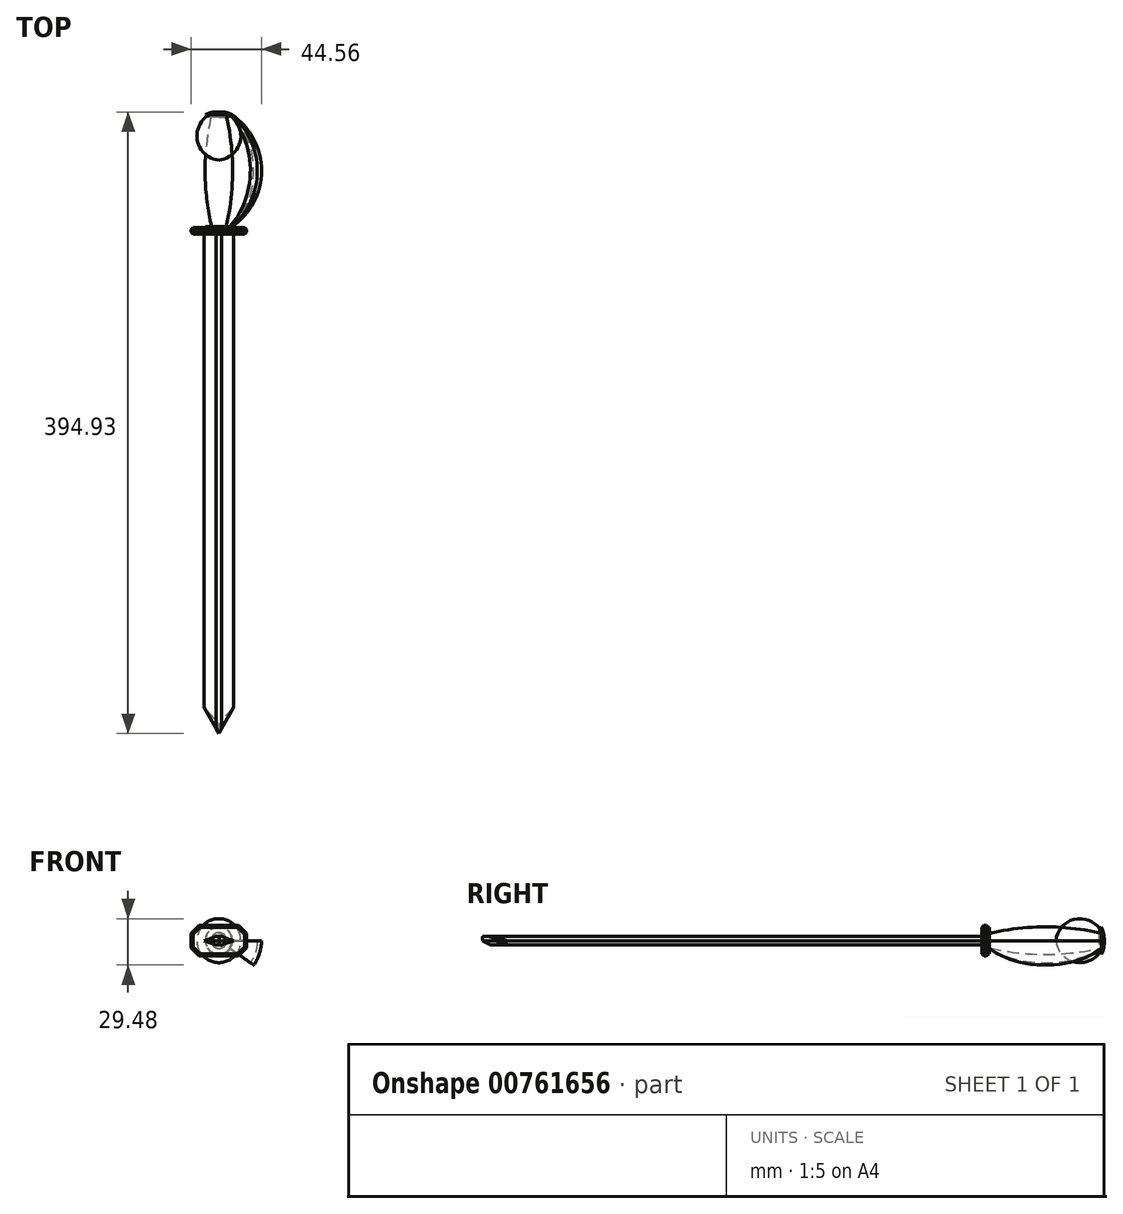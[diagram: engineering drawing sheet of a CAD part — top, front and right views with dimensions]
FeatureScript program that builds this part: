
annotation { "Feature Type Name" : "Feature", "Feature Type Description" : "" }
export const myFeature = defineFeature(function(context is Context, id is Id, definition is map)
    precondition{}
    {
        {
            var Q0;
            Q0=qCreatedBy(makeId("Top.planeOp"),FACE);
            var sketch = newSketch(context, id + "F0", { "sketchPlane" : qUnion([Q0])});
            skLineSegment(sketch, "E0.bottom", {"start": v(0, -33.84) * mm, "end": v(18.2, -33.84) * mm});
            skLineSegment(sketch, "E0.top", {"start": v(0, 37.15) * mm, "end": v(18.2, 37.15) * mm});
            skLineSegment(sketch, "E0.left", {"start": v(0, -33.84) * mm, "end": v(0, 37.15) * mm});
            skLineSegment(sketch, "E0.right", {"start": v(18.2, -33.84) * mm, "end": v(18.2, 37.15) * mm});
            skArc(sketch, "E1", {"start": v(4.66, -33.84) * mm, "mid": v(8.75, 1.65) * mm, "end": v(4.66, 37.15) * mm});
            skSolve(sketch);
        }
        {
            var Q0;
            {var subQ0=sQuery(id+"F0.wireOp",EDGE,"E0.left");Q0=makeQuery(id+"F0.imprint","IMPRINT",FACE,{"disambiguationData":[TD([[makeQuery(id+"F0.imprint","IMPRINT",EDGE,{"derivedFrom":subQ0}),-1.0]])]});}
            var Q1;
            Q1=sQuery(id+"F0.wireOp",EDGE,"E0.left");
            revolve(context, id + "F1", {"surfaceOperationType" : NewSurfaceOperationType.NEW, "entities" : qUnion([Q0]), "axis" : qUnion([Q1]), "revolveType" : RevolveType.FULL});
        }
        {
            var Q0;
            Q0=qCreatedBy(makeId("Top.planeOp"),FACE);
            var sketch = newSketch(context, id + "F2", { "sketchPlane" : qUnion([Q0])});
            skLineSegment(sketch, "E2", {"start": v(0, 37.15) * mm, "end": v(0, 38.92) * mm});
            skArc(sketch, "E3", {"start": v(8.61, 37.15) * mm, "mid": v(4.43, 38.66) * mm, "end": v(0, 38.92) * mm});
            skArc(sketch, "E4.MirrorCS", {"start": v(8.61, 37.15) * mm, "mid": v(4.43, 35.63) * mm, "end": v(0, 35.38) * mm});
            skLineSegment(sketch, "E5.MirrorCS", {"start": v(0, 37.15) * mm, "end": v(0, 35.38) * mm});
            skSolve(sketch);
        }
        {
            var Q0;
            Q0=makeQuery(id+"F2.imprint","IMPRINT",FACE,{"disambiguationData":[TD([[makeQuery(id+"F2.imprint","IMPRINT",EDGE,{"derivedFrom":sQuery(id+"F2.wireOp",EDGE,"E2")}),-1.0]])]});
            var Q1;
            Q1=sQuery(id+"F2.wireOp",EDGE,"E2");
            revolve(context, id + "F3", {"surfaceOperationType" : NewSurfaceOperationType.NEW, "entities" : qUnion([Q0]), "axis" : qUnion([Q1]), "revolveType" : RevolveType.FULL});
        }
        {
            var Q0;
            Q0=qCreatedBy(makeId("Top.planeOp"),FACE);
            var sketch = newSketch(context, id + "F4", { "sketchPlane" : qUnion([Q0])});
            skLineSegment(sketch, "E6", {"start": v(8.17, 37.23) * mm, "end": v(8.17, 37.36) * mm});
            skLineSegment(sketch, "E7", {"start": v(8.17, 37.36) * mm, "end": v(8.17, 36.95) * mm});
            skArc(sketch, "E8", {"start": v(8.17, -34.23) * mm, "mid": v(27.04, 1.57) * mm, "end": v(8.17, 37.36) * mm});
            skArc(sketch, "E9", {"start": v(8.17, -33.85) * mm, "mid": v(24.4, 1.55) * mm, "end": v(8.17, 36.95) * mm});
            skLineSegment(sketch, "E10.trimOffspring", {"start": v(8.17, -33.85) * mm, "end": v(8.17, -34.23) * mm});
            skSolve(sketch);
        }
        {
            var Q0;
            {var subQ0=sQuery(id+"F4.wireOp",EDGE,"E8");Q0=makeQuery(id+"F4.imprint","IMPRINT",FACE,{"disambiguationData":[TD([[makeQuery(id+"F4.imprint","IMPRINT",EDGE,{"derivedFrom":subQ0}),1.0]])]});}
            var Q1;
            Q1=sQuery(id+"F0.wireOp",EDGE,"E0.left");
            revolve(context, id + "F5", {"operationType" : NewBodyOperationType.ADD, "surfaceOperationType" : NewSurfaceOperationType.NEW, "entities" : qUnion([Q0]), "axis" : qUnion([Q1]), "revolveType" : RevolveType.ONE_DIRECTION, "angle" : 35 * degree});
        }
        {
            var Q0;
            Q0=makeQuery(id+"F1.opRevolve","SWEPT_FACE",FACE,{"disambiguationData":[OSD([sQuery(id+"F0.wireOp",EDGE,"E0.bottom")])]});
            var sketch = newSketch(context, id + "F6", { "sketchPlane" : qUnion([Q0])});
            skCircle(sketch, "E11", {"center": v(0, 0) * mm, "radius": 8.51 * mm});
            skLineSegment(sketch, "E12.bottom", {"start": v(-13.18, 9.67) * mm, "end": v(13.18, 9.67) * mm});
            skLineSegment(sketch, "E12.top", {"start": v(-13.18, -9.67) * mm, "end": v(13.18, -9.67) * mm});
            skLineSegment(sketch, "E12.left", {"start": v(-13.18, 9.67) * mm, "end": v(-13.18, -9.67) * mm});
            skLineSegment(sketch, "E12.right", {"start": v(13.18, 9.67) * mm, "end": v(13.18, -9.67) * mm});
            skSolve(sketch);
        }
        {
            var Q0;
            Q0=makeQuery(id+"F6.imprint","IMPRINT",FACE,{"disambiguationData":[TD([[makeQuery(id+"F6.imprint","IMPRINT",EDGE,{"derivedFrom":sQuery(id+"F6.wireOp",EDGE,"E11")}),1.0]])]});
            var Q1;
            Q1=makeQuery(id+"F6.imprint","IMPRINT",FACE,{"disambiguationData":[TD([[makeQuery(id+"F6.imprint","IMPRINT",EDGE,{"derivedFrom":makeQuery(id+"F1.opRevolve","SWEPT_EDGE",EDGE,{"disambiguationData":[OSD([sQuery(id+"F0.wireOp",EDGE,"E0.bottom"),sQuery(id+"F0.wireOp",EDGE,"E1")])]})}),1.0]])]});
            extrude(context, id + "F7", {"entities" : qUnion([Q0, Q1]), "operationType" : NewBodyOperationType.ADD, "depth" : 0.76 * mm, "offsetDistance" : 25.4 * mm});
        }
        {
            var Q0;
            Q0=makeQuery(id+"F7.opExtrude","CAP_FACE",FACE,{"disambiguationData":[OSD([sQuery(id+"F6.wireOp",EDGE,"E11")])],"isStart":false});
            var sketch = newSketch(context, id + "F8", { "sketchPlane" : qUnion([Q0])});
            skLineSegment(sketch, "E13.bottom", {"start": v(17.52, 9.72) * mm, "end": v(-17.52, 9.72) * mm});
            skLineSegment(sketch, "E13.top", {"start": v(17.52, -9.72) * mm, "end": v(-17.52, -9.72) * mm});
            skLineSegment(sketch, "E13.left", {"start": v(17.52, 9.72) * mm, "end": v(17.52, -9.72) * mm});
            skLineSegment(sketch, "E13.right", {"start": v(-17.52, 9.72) * mm, "end": v(-17.52, -9.72) * mm});
            skPoint(sketch, "E13.middle", {"position": v(0, 0) * mm});
            skSolve(sketch);
        }
        {
            var Q0;
            Q0=makeQuery(id+"F8.imprint","IMPRINT",FACE,{"disambiguationData":[TD([[makeQuery(id+"F8.imprint","IMPRINT",EDGE,{"derivedFrom":sQuery(id+"F8.wireOp",EDGE,"E13.bottom")}),1.0]])]});
            var Q1;
            Q1=makeQuery(id+"F8.imprint","IMPRINT",FACE,{"disambiguationData":[TD([[makeQuery(id+"F8.imprint","IMPRINT",EDGE,{"derivedFrom":makeQuery(id+"F7.opExtrude","CAP_EDGE",EDGE,{"disambiguationData":[OSD([sQuery(id+"F6.wireOp",EDGE,"E11")])],"isStart":false})}),1.0]])]});
            extrude(context, id + "F9", {"entities" : qUnion([Q0, Q1]), "depth" : 4.06 * mm, "offsetDistance" : 25.4 * mm});
        }
        {
            var Q0;
            Q0=makeQuery(id+"F9.opExtrude","SWEPT_EDGE",EDGE,{"disambiguationData":[OSD([sQuery(id+"F8.wireOp",EDGE,"E13.bottom"),sQuery(id+"F8.wireOp",EDGE,"E13.right")])]});
            var Q1;
            Q1=makeQuery(id+"F9.opExtrude","SWEPT_EDGE",EDGE,{"disambiguationData":[OSD([sQuery(id+"F8.wireOp",EDGE,"E13.top"),sQuery(id+"F8.wireOp",EDGE,"E13.right")])]});
            var Q2;
            Q2=makeQuery(id+"F9.opExtrude","SWEPT_EDGE",EDGE,{"disambiguationData":[OSD([sQuery(id+"F8.wireOp",EDGE,"E13.bottom"),sQuery(id+"F8.wireOp",EDGE,"E13.left")])]});
            var Q3;
            Q3=makeQuery(id+"F9.opExtrude","SWEPT_EDGE",EDGE,{"disambiguationData":[OSD([sQuery(id+"F8.wireOp",EDGE,"E13.top"),sQuery(id+"F8.wireOp",EDGE,"E13.left")])]});
            chamfer(context, id + "F10", {"entities" : qUnion([Q0, Q1, Q2, Q3]), "width" : 5.08 * mm, "tangentPropagation" : true});
        }
        {
            var Q0;
            Q0=makeQuery(id+"F9.opExtrude","CAP_FACE",FACE,{"disambiguationData":[OSD([sQuery(id+"F8.wireOp",EDGE,"E13.bottom"),sQuery(id+"F8.wireOp",EDGE,"E13.top"),sQuery(id+"F8.wireOp",EDGE,"E13.left"),sQuery(id+"F8.wireOp",EDGE,"E13.right")])],"isStart":false});
            var Q1;
            Q1=makeQuery(id+"F9.opExtrude","CAP_FACE",FACE,{"disambiguationData":[OSD([sQuery(id+"F8.wireOp",EDGE,"E13.bottom"),sQuery(id+"F8.wireOp",EDGE,"E13.top"),sQuery(id+"F8.wireOp",EDGE,"E13.left"),sQuery(id+"F8.wireOp",EDGE,"E13.right")])],"isStart":true});
            chamfer(context, id + "F11", {"entities" : qUnion([Q0, Q1]), "width" : 1.27 * mm, "tangentPropagation" : true});
        }
        {
            var Q0;
            Q0=makeQuery(id+"F9.opExtrude","CAP_FACE",FACE,{"disambiguationData":[OSD([sQuery(id+"F8.wireOp",EDGE,"E13.bottom"),sQuery(id+"F8.wireOp",EDGE,"E13.top"),sQuery(id+"F8.wireOp",EDGE,"E13.left"),sQuery(id+"F8.wireOp",EDGE,"E13.right")])],"isStart":false});
            var sketch = newSketch(context, id + "F12", { "sketchPlane" : qUnion([Q0])});
            skLineSegment(sketch, "E14.bottom", {"start": v(9.47, 2.56) * mm, "end": v(-9.47, 2.56) * mm});
            skLineSegment(sketch, "E14.top", {"start": v(9.47, -2.56) * mm, "end": v(-9.47, -2.56) * mm});
            skLineSegment(sketch, "E14.left", {"start": v(9.47, 2.56) * mm, "end": v(9.47, -2.56) * mm});
            skLineSegment(sketch, "E14.right", {"start": v(-9.47, 2.56) * mm, "end": v(-9.47, -2.56) * mm});
            skPoint(sketch, "E14.middle", {"position": v(0, 0) * mm});
            skSolve(sketch);
        }
        {
            var Q0;
            Q0=makeQuery(id+"F12.imprint","IMPRINT",FACE,{"disambiguationData":[TD([[makeQuery(id+"F12.imprint","IMPRINT",EDGE,{"derivedFrom":sQuery(id+"F12.wireOp",EDGE,"E14.bottom")}),1.0]])]});
            extrude(context, id + "F13", {"entities" : qUnion([Q0]), "depth" : 320.04 * mm, "offsetDistance" : 25.4 * mm});
        }
        {
            var Q0;
            Q0=makeQuery(id+"F13.opExtrude","SWEPT_EDGE",EDGE,{"disambiguationData":[OSD([sQuery(id+"F12.wireOp",EDGE,"E14.bottom"),sQuery(id+"F12.wireOp",EDGE,"E14.right")])]});
            var Q1;
            Q1=makeQuery(id+"F13.opExtrude","SWEPT_EDGE",EDGE,{"disambiguationData":[OSD([sQuery(id+"F12.wireOp",EDGE,"E14.bottom"),sQuery(id+"F12.wireOp",EDGE,"E14.left")])]});
            var Q2;
            Q2=makeQuery(id+"F13.opExtrude","SWEPT_EDGE",EDGE,{"disambiguationData":[OSD([sQuery(id+"F12.wireOp",EDGE,"E14.top"),sQuery(id+"F12.wireOp",EDGE,"E14.right")])]});
            var Q3;
            Q3=makeQuery(id+"F13.opExtrude","SWEPT_EDGE",EDGE,{"disambiguationData":[OSD([sQuery(id+"F12.wireOp",EDGE,"E14.top"),sQuery(id+"F12.wireOp",EDGE,"E14.left")])]});
            chamfer(context, id + "F14", {"entities" : qUnion([Q0, Q1, Q2, Q3]), "chamferType" : ChamferType.TWO_OFFSETS, "width1" : 2.56 * mm, "oppositeDirection" : false, "width2" : 7.62 * mm, "tangentPropagation" : true});
        }
        {
            var Q0;
            Q0=makeQuery(id+"F13.opExtrude","SWEPT_FACE",FACE,{"disambiguationData":[OSD([sQuery(id+"F12.wireOp",EDGE,"E14.bottom")])]});
            var sketch = newSketch(context, id + "F15", { "sketchPlane" : qUnion([Q0])});
            skLineSegment(sketch, "E15", {"start": v(0, -355.95) * mm, "end": v(11.37, -336) * mm});
            skLineSegment(sketch, "E16.MirrorCS", {"start": v(0, -355.95) * mm, "end": v(-11.37, -336) * mm});
            skLineSegment(sketch, "E17", {"start": v(-11.37, -336) * mm, "end": v(-10.94, -359.44) * mm});
            skLineSegment(sketch, "E18", {"start": v(-10.94, -359.44) * mm, "end": v(13.79, -359.44) * mm});
            skLineSegment(sketch, "E19", {"start": v(13.79, -359.44) * mm, "end": v(11.37, -336) * mm});
            skSolve(sketch);
        }
        {
            var Q0;
            {var subQ0=sQuery(id+"F15.wireOp",EDGE,"E17");Q0=makeQuery(id+"F15.imprint","IMPRINT",FACE,{"disambiguationData":[TD([[makeQuery(id+"F15.imprint","IMPRINT",EDGE,{"derivedFrom":subQ0}),1.0]])]});}
            var Q1;
            {var subQ0=sQuery(id+"F12.wireOp",EDGE,"E14.bottom");var subQ1=makeQuery(id+"F13.opExtrude","CAP_EDGE",EDGE,{"disambiguationData":[OSD([subQ0])],"isStart":false});Q1=makeQuery(id+"F15.imprint","IMPRINT",FACE,{"disambiguationData":[TD([[makeQuery(id+"F15.imprint","IMPRINT",EDGE,{"derivedFrom":subQ1}),-1.0]])]});}
            extrude(context, id + "F16", {"entities" : qUnion([Q0, Q1]), "operationType" : NewBodyOperationType.REMOVE, "oppositeDirection" : true, "depth" : 25.4 * mm, "offsetDistance" : 25.4 * mm});
        }
        {
            var Q0;
            Q0=makeQuery(id+"F16.boolean.opBoolean","COPY",EDGE,{"derivedFrom":makeQuery(id+"F16.opExtrude","CAP_EDGE",EDGE,{"disambiguationData":[OSD([sQuery(id+"F15.wireOp",EDGE,"E16.MirrorCS")])],"isStart":true})});
            var Q1;
            Q1=makeQuery(id+"F16.boolean.opBoolean","INTERSECT",EDGE,{"derivedFrom":[makeQuery(id+"F13.opExtrude","SWEPT_FACE",FACE,{"disambiguationData":[OSD([sQuery(id+"F12.wireOp",EDGE,"E14.top")])]}),makeQuery(id+"F16.opExtrude","SWEPT_FACE",FACE,{"disambiguationData":[OSD([sQuery(id+"F15.wireOp",EDGE,"E16.MirrorCS")])]})]});
            var Q2;
            Q2=makeQuery(id+"F16.boolean.opBoolean","COPY",EDGE,{"derivedFrom":makeQuery(id+"F16.opExtrude","CAP_EDGE",EDGE,{"disambiguationData":[OSD([sQuery(id+"F15.wireOp",EDGE,"E15")])],"isStart":true})});
            var Q3;
            Q3=makeQuery(id+"F16.boolean.opBoolean","INTERSECT",EDGE,{"derivedFrom":[makeQuery(id+"F13.opExtrude","SWEPT_FACE",FACE,{"disambiguationData":[OSD([sQuery(id+"F12.wireOp",EDGE,"E14.top")])]}),makeQuery(id+"F16.opExtrude","SWEPT_FACE",FACE,{"disambiguationData":[OSD([sQuery(id+"F15.wireOp",EDGE,"E15")])]})]});
            chamfer(context, id + "F17", {"entities" : qUnion([Q0, Q1, Q2, Q3]), "chamferType" : ChamferType.TWO_OFFSETS, "width1" : 2.56 * mm, "oppositeDirection" : false, "width2" : 2.56 * mm, "tangentPropagation" : true});
        }
    });
